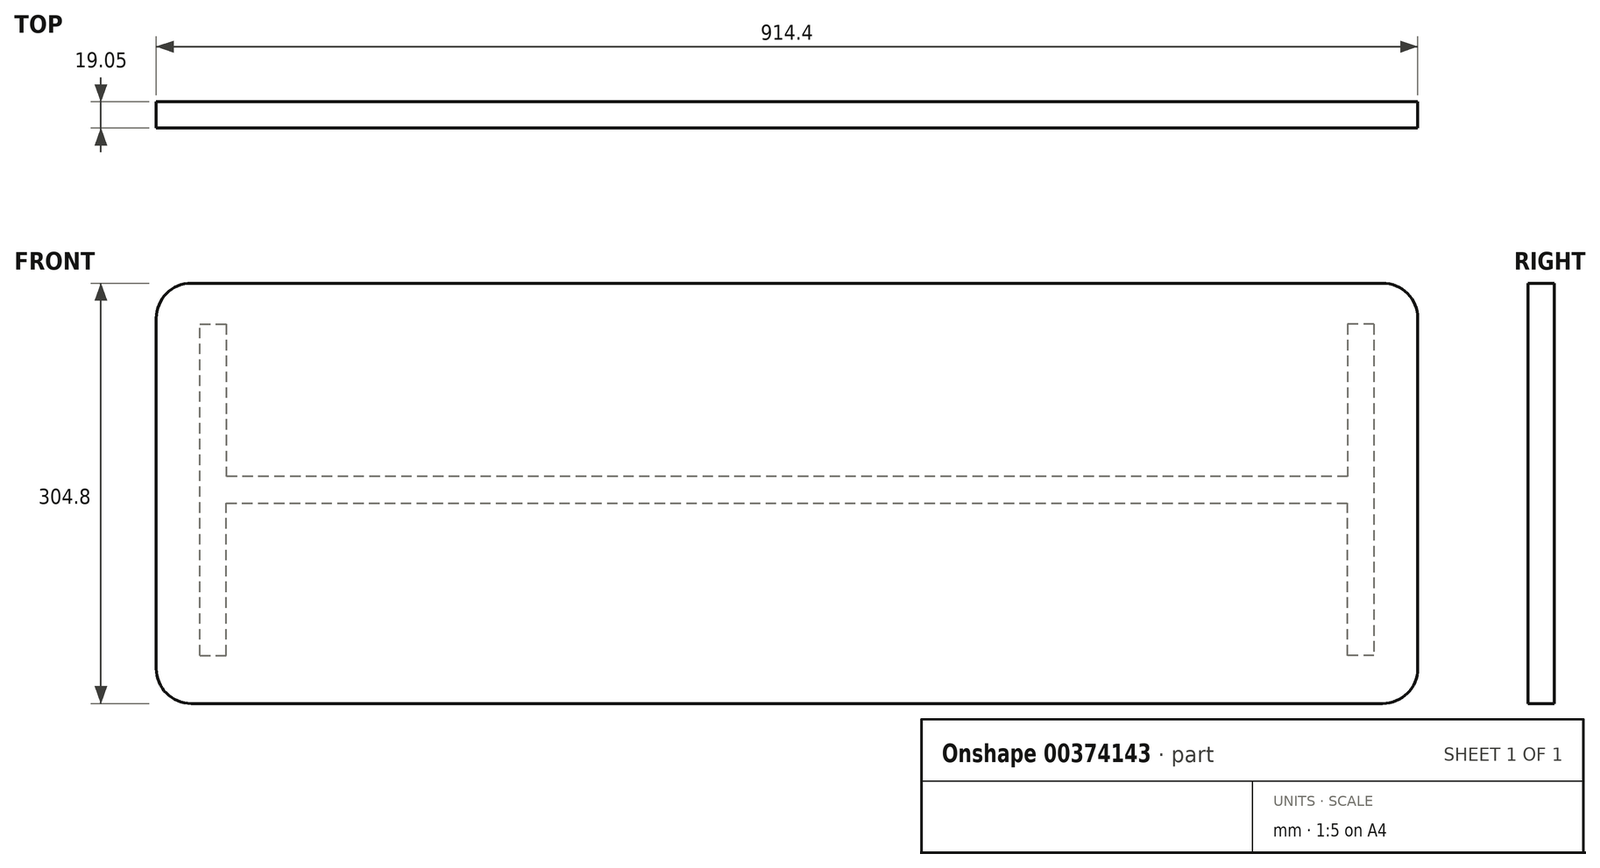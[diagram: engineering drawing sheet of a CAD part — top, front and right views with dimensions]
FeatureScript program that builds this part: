
annotation { "Feature Type Name" : "Feature", "Feature Type Description" : "" }
export const myFeature = defineFeature(function(context is Context, id is Id, definition is map)
    precondition{}
    {
        {
            var Q0;
            Q0=qCreatedBy(makeId("Front.planeOp"),FACE);
            var sketch = newSketch(context, id + "F0", { "sketchPlane" : qUnion([Q0])});
            skLineSegment(sketch, "E0", {"start": v(0, 163.43) * mm, "end": v(457.2, 163.43) * mm});
            skLineSegment(sketch, "E1", {"start": v(457.2, 163.43) * mm, "end": v(457.2, -141.37) * mm});
            skLineSegment(sketch, "E2", {"start": v(457.2, -141.37) * mm, "end": v(0, -141.37) * mm});
            skLineSegment(sketch, "E3", {"start": v(0, 163.43) * mm, "end": v(0, -141.37) * mm, "construction": true});
            skLineSegment(sketch, "E4.MirrorCS", {"start": v(0, 163.43) * mm, "end": v(-457.2, 163.43) * mm});
            skLineSegment(sketch, "E5.MirrorCS", {"start": v(-457.2, 163.43) * mm, "end": v(-457.2, -141.37) * mm});
            skLineSegment(sketch, "E6.MirrorCS", {"start": v(-457.2, -141.37) * mm, "end": v(0, -141.37) * mm});
            skSolve(sketch);
        }
        {
            var Q0;
            Q0=qSketchRegion(id+"F0",true);
            extrude(context, id + "F1", {"entities" : qUnion([Q0]), "depth" : 19.05 * mm});
        }
        {
            var Q0;
            Q0=qCreatedBy(makeId("Front.planeOp"),FACE);
            var sketch = newSketch(context, id + "F2", { "sketchPlane" : qUnion([Q0])});
            skLineSegment(sketch, "E7", {"start": v(-166.8, 13.7) * mm, "end": v(0, 13.7) * mm, "construction": true});
            skLineSegment(sketch, "E8", {"start": v(0, -142.51) * mm, "end": v(0, 164.75) * mm, "construction": true});
            skLineSegment(sketch, "E9", {"start": v(0, 13.7) * mm, "end": v(165.2, 13.7) * mm, "construction": true});
            skLineSegment(sketch, "E10", {"start": v(425.45, 13.7) * mm, "end": v(425.45, 133.83) * mm});
            skLineSegment(sketch, "E11", {"start": v(425.45, 133.83) * mm, "end": v(406.4, 133.83) * mm});
            skLineSegment(sketch, "E12", {"start": v(406.4, 133.83) * mm, "end": v(406.4, 13.7) * mm});
            skLineSegment(sketch, "E13.MirrorCS", {"start": v(406.4, -106.45) * mm, "end": v(406.4, 13.7) * mm});
            skLineSegment(sketch, "E14.MirrorCS", {"start": v(425.45, 13.7) * mm, "end": v(425.45, -106.45) * mm});
            skLineSegment(sketch, "E15.MirrorCS", {"start": v(425.45, -106.45) * mm, "end": v(406.4, -106.45) * mm});
            skLineSegment(sketch, "E16.MirrorCS", {"start": v(-406.4, 133.83) * mm, "end": v(-406.4, 13.7) * mm});
            skLineSegment(sketch, "E17.MirrorCS", {"start": v(-425.45, 133.83) * mm, "end": v(-406.4, 133.83) * mm});
            skLineSegment(sketch, "E18.MirrorCS", {"start": v(-425.45, 13.7) * mm, "end": v(-425.45, 133.83) * mm});
            skLineSegment(sketch, "E19.MirrorCS", {"start": v(-425.45, 13.7) * mm, "end": v(-425.45, -106.45) * mm});
            skLineSegment(sketch, "E20.MirrorCS", {"start": v(-406.4, -106.45) * mm, "end": v(-406.4, 13.7) * mm});
            skLineSegment(sketch, "E21.MirrorCS", {"start": v(-425.45, -106.45) * mm, "end": v(-406.4, -106.45) * mm});
            skLineSegment(sketch, "E22", {"start": v(110.9, 13.7) * mm, "end": v(110.9, 23.34) * mm, "construction": true});
            skLineSegment(sketch, "E23.MirrorCS", {"start": v(110.9, 13.7) * mm, "end": v(110.9, 4.04) * mm, "construction": true});
            skLineSegment(sketch, "E24", {"start": v(406.4, 23.34) * mm, "end": v(-406.4, 23.34) * mm});
            skLineSegment(sketch, "E25", {"start": v(-406.4, 23.34) * mm, "end": v(-406.4, 4.04) * mm});
            skLineSegment(sketch, "E26", {"start": v(-406.4, 4.04) * mm, "end": v(406.4, 4.04) * mm});
            skLineSegment(sketch, "E27", {"start": v(406.4, 4.04) * mm, "end": v(406.4, 23.34) * mm});
            skLineSegment(sketch, "E28", {"start": v(0, 133.83) * mm, "end": v(-9.52, 133.83) * mm, "construction": true});
            skLineSegment(sketch, "E29.MirrorCS", {"start": v(0, 133.83) * mm, "end": v(9.52, 133.83) * mm, "construction": true});
            skLineSegment(sketch, "E30", {"start": v(-9.52, 133.83) * mm, "end": v(-9.53, -106.45) * mm, "construction": true});
            skLineSegment(sketch, "E31", {"start": v(-9.53, -106.45) * mm, "end": v(0, -106.45) * mm, "construction": true});
            skLineSegment(sketch, "E32.MirrorCS", {"start": v(9.53, -106.45) * mm, "end": v(0, -106.45) * mm, "construction": true});
            skLineSegment(sketch, "E33.MirrorCS", {"start": v(9.52, 133.83) * mm, "end": v(9.53, -106.45) * mm, "construction": true});
            skLineSegment(sketch, "E34", {"start": v(415.93, 133.83) * mm, "end": v(9.53, 133.83) * mm, "construction": true});
            skLineSegment(sketch, "E35.trimOffspring", {"start": v(-9.52, 133.83) * mm, "end": v(-415.93, 133.83) * mm, "construction": true});
            skSolve(sketch);
        }
        {
            var Q0;
            Q0=qSketchRegion(id+"F2",true);
            extrude(context, id + "F3", {"entities" : qUnion([Q0]), "operationType" : NewBodyOperationType.REMOVE, "depth" : 3 / 203.2 * mm});
        }
        {
            var Q0;
            Q0=makeQuery(id+"F1.opExtrude","SWEPT_EDGE",EDGE,{"disambiguationData":[OSD([sQuery(id+"F0.wireOp",EDGE,"E0"),sQuery(id+"F0.wireOp",EDGE,"E1")])]});
            fillet(context, id + "F4", {"entities" : qUnion([Q0]), "radius" : 25.4 * mm, "tangentPropagation" : true, "allowEdgeOverflow" : false});
        }
        {
            var Q0;
            Q0=makeQuery(id+"F1.opExtrude","SWEPT_EDGE",EDGE,{"disambiguationData":[OSD([sQuery(id+"F0.wireOp",EDGE,"E1"),sQuery(id+"F0.wireOp",EDGE,"E2")])]});
            fillet(context, id + "F5", {"entities" : qUnion([Q0]), "radius" : 25.4 * mm, "tangentPropagation" : true, "allowEdgeOverflow" : false});
        }
        {
            var Q0;
            Q0=makeQuery(id+"F1.opExtrude","SWEPT_EDGE",EDGE,{"disambiguationData":[OSD([sQuery(id+"F0.wireOp",EDGE,"E4.MirrorCS"),sQuery(id+"F0.wireOp",EDGE,"E5.MirrorCS")])]});
            fillet(context, id + "F6", {"entities" : qUnion([Q0]), "radius" : 25.4 * mm, "tangentPropagation" : true, "allowEdgeOverflow" : false});
        }
        {
            var Q0;
            Q0=makeQuery(id+"F1.opExtrude","SWEPT_EDGE",EDGE,{"disambiguationData":[OSD([sQuery(id+"F0.wireOp",EDGE,"E5.MirrorCS"),sQuery(id+"F0.wireOp",EDGE,"E6.MirrorCS")])]});
            fillet(context, id + "F7", {"entities" : qUnion([Q0]), "radius" : 25.4 * mm, "tangentPropagation" : true, "allowEdgeOverflow" : false});
        }
    });
